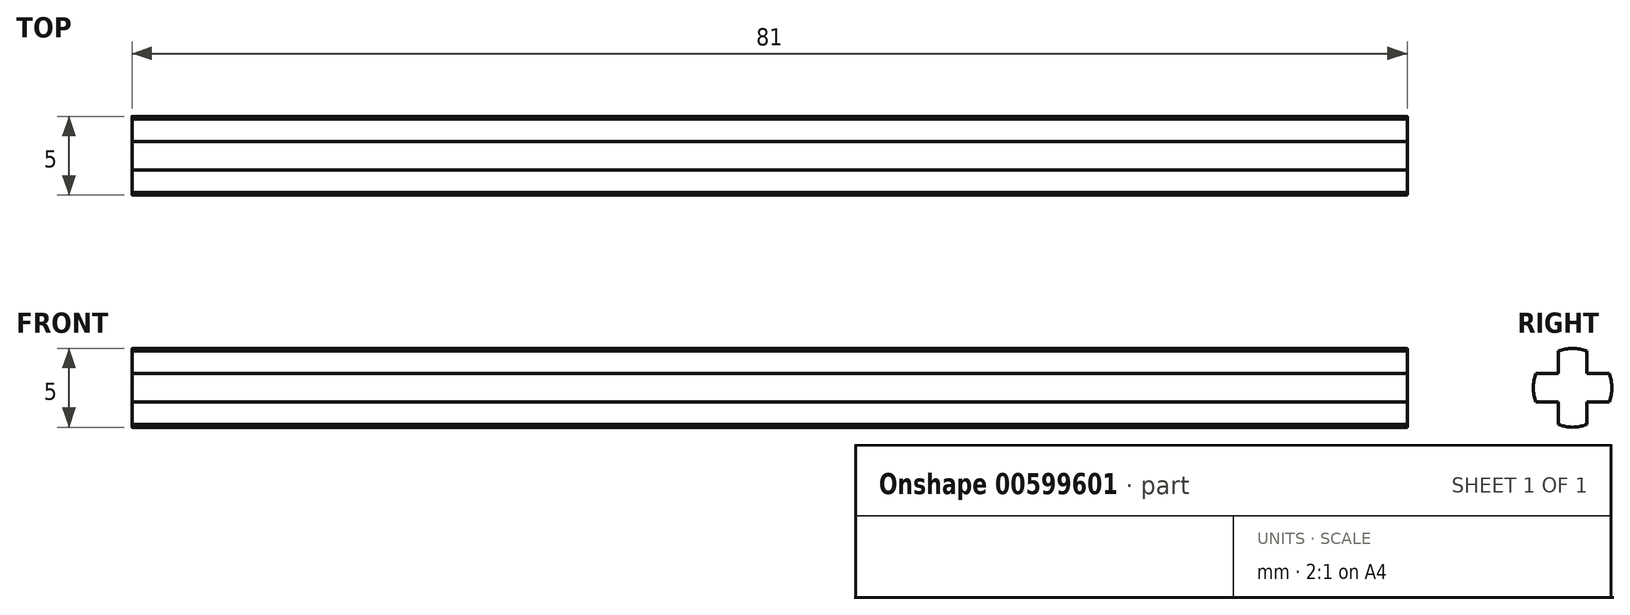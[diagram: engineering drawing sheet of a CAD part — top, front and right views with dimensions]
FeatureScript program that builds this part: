
annotation { "Feature Type Name" : "Feature", "Feature Type Description" : "" }
export const myFeature = defineFeature(function(context is Context, id is Id, definition is map)
    precondition{}
    {
        {
            var Q0;
            Q0=qCreatedBy(makeId("Right.planeOp"),FACE);
            var sketch = newSketch(context, id + "F0", { "sketchPlane" : qUnion([Q0])});
            skArc(sketch, "E0", {"start": v(2.33, -0.9) * mm, "mid": v(2.5, 0) * mm, "end": v(2.33, 0.9) * mm});
            skLineSegment(sketch, "E1.left", {"start": v(-0.9, 2.33) * mm, "end": v(-0.9, 0.9) * mm});
            skLineSegment(sketch, "E1.right", {"start": v(0.9, 2.33) * mm, "end": v(0.9, 0.9) * mm});
            skLineSegment(sketch, "E2.bottom", {"start": v(2.33, 0.9) * mm, "end": v(0.9, 0.9) * mm});
            skLineSegment(sketch, "E2.top", {"start": v(2.33, -0.9) * mm, "end": v(0.9, -0.9) * mm});
            skArc(sketch, "E3.trimOffspring", {"start": v(0.9, 2.33) * mm, "mid": v(0, 2.5) * mm, "end": v(-0.9, 2.33) * mm});
            skArc(sketch, "E4.trimOffspring", {"start": v(-2.33, 0.9) * mm, "mid": v(-2.5, 0) * mm, "end": v(-2.33, -0.9) * mm});
            skArc(sketch, "E5.trimOffspring", {"start": v(-0.9, -2.33) * mm, "mid": v(0, -2.5) * mm, "end": v(0.9, -2.33) * mm});
            skLineSegment(sketch, "E6.trimOffspring", {"start": v(-0.9, -0.9) * mm, "end": v(-0.9, -2.33) * mm});
            skLineSegment(sketch, "E7.trimOffspring", {"start": v(-0.9, 0.9) * mm, "end": v(-2.33, 0.9) * mm});
            skLineSegment(sketch, "E8.trimOffspring", {"start": v(0.9, -0.9) * mm, "end": v(0.9, -2.33) * mm});
            skLineSegment(sketch, "E9.trimOffspring", {"start": v(-0.9, -0.9) * mm, "end": v(-2.33, -0.9) * mm});
            skSolve(sketch);
        }
        {
            var Q0;
            Q0 = qSketchRegion(id + "F0", true);
            extrude(context, id + "F1", {"entities" : qUnion([Q0]), "depth" : 81 * mm, "offsetDistance" : 25 * mm});
        }
    });
